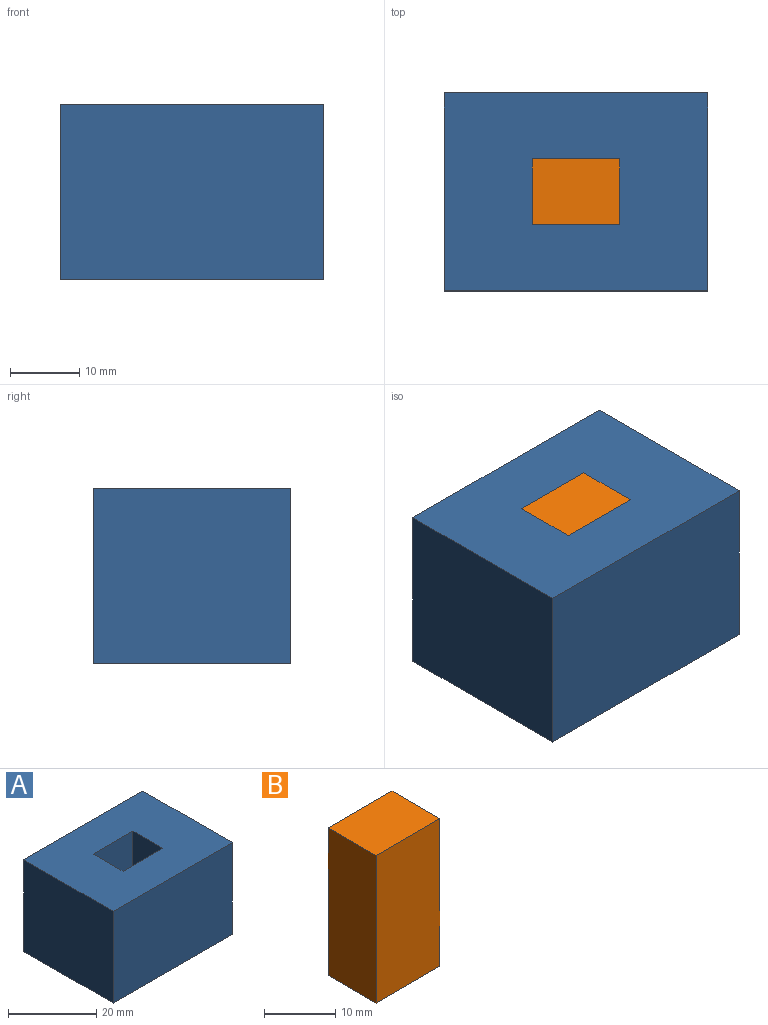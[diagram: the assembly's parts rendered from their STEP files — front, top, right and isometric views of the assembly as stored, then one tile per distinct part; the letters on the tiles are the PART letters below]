
ASSEMBLY  parts=2 mates=1
PART A: 10 faces, bbox 38.1x28.6x25.4 mm
  f0: plane 38.1x28.58mm, normal (0,0,1), area 967.7mm2, adj f1,f2,f4,f5,f6,f7,f8,f9
  f1: plane 25.4x9.53mm, normal (1,0,0), area 241.9mm2, adj f0,f3,f4,f5
  f2: plane 28.58x25.4mm, normal (-1,0,0), area 725.8mm2, adj f0,f3,f7,f8
  f3: plane 38.1x28.58mm, normal (0,0,-1), area 967.7mm2, adj f1,f2,f4,f5,f6,f7,f8,f9
  f4: plane 25.4x12.7mm, normal (0,-1,0), area 322.6mm2, adj f0,f1,f3,f6
  f5: plane 25.4x12.7mm, normal (0,1,0), area 322.6mm2, adj f0,f1,f3,f6
  f6: plane 25.4x9.53mm, normal (-1,0,0), area 241.9mm2, adj f0,f3,f4,f5
  f7: plane 38.1x25.4mm, normal (0,-1,0), area 967.7mm2, adj f0,f2,f3,f9
  f8: plane 38.1x25.4mm, normal (0,1,0), area 967.7mm2, adj f0,f2,f3,f9
  f9: plane 28.58x25.4mm, normal (1,0,0), area 725.8mm2, adj f0,f3,f7,f8
PART B: 6 faces, bbox 12.7x9.5x25.4 mm
  f0: plane 25.4x9.53mm, normal (-1,0,0), area 241.9mm2, adj f1,f3,f4,f5
  f1: plane 25.4x12.7mm, normal (0,-1,0), area 322.6mm2, adj f0,f2,f4,f5
  f2: plane 25.4x9.53mm, normal (1,0,0), area 241.9mm2, adj f1,f3,f4,f5
  f3: plane 25.4x12.7mm, normal (0,1,0), area 322.6mm2, adj f0,f2,f4,f5
  f4: plane 12.7x9.53mm, normal (0,0,1), area 121mm2, adj f0,f1,f2,f3
  f5: plane 12.7x9.53mm, normal (0,0,-1), area 121mm2, adj f0,f1,f2,f3
PLACE A at identity
PLACE B at identity fixed
MATE fastened B.f4 <-> A.f0  axis (0,0,1) through (0,0,25.4)mm
